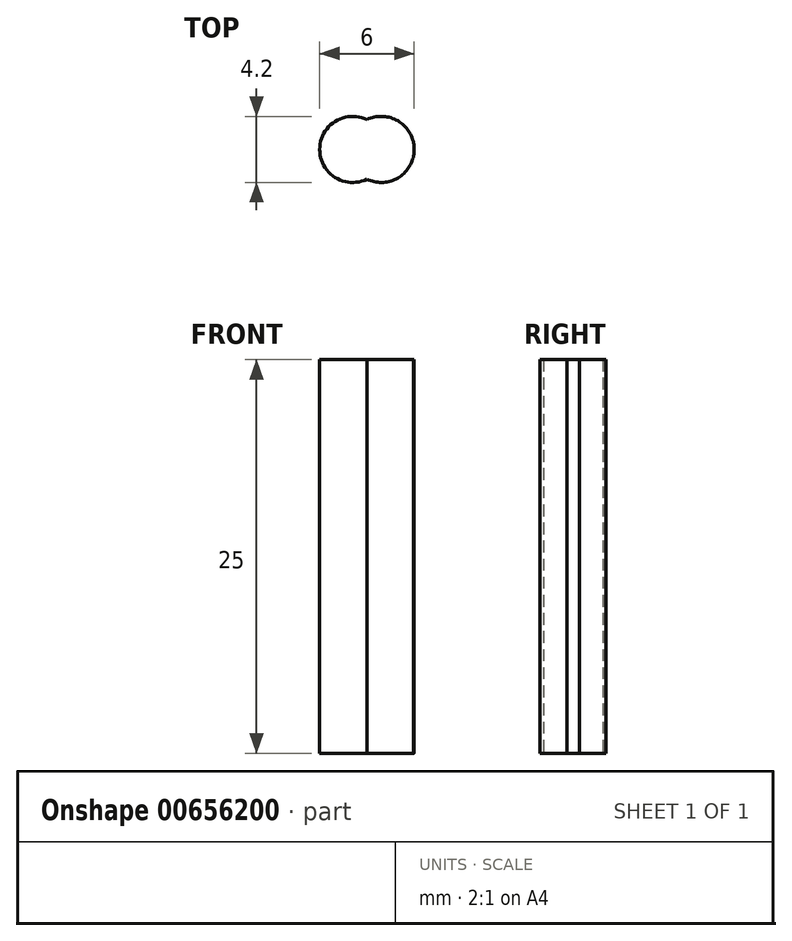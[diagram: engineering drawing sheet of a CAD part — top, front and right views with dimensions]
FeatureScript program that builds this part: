
annotation { "Feature Type Name" : "Feature", "Feature Type Description" : "" }
export const myFeature = defineFeature(function(context is Context, id is Id, definition is map)
    precondition{}
    {
        {
            var Q0;
            Q0=qCreatedBy(makeId("Top.planeOp"),FACE);
            var sketch = newSketch(context, id + "F0", { "sketchPlane" : qUnion([Q0])});
            skCircle(sketch, "E0", {"center": v(0, 0) * mm, "radius": 3 * mm});
            skCircle(sketch, "E1", {"center": v(-0.9, 0) * mm, "radius": 2.1 * mm});
            skCircle(sketch, "E2", {"center": v(0.91, 0) * mm, "radius": 2.1 * mm});
            skSolve(sketch);
        }
        {
            var Q0;
            {var subQ0=sQuery(id+"F0.wireOp",EDGE,"E2");var subQ1=sQuery(id+"F0.wireOp",EDGE,"E0");var subQ2=makeQuery(id+"F0.imprint","INTERSECT",VERTEX,{"disambiguationData":[OD(0.0)],"derivedFrom":[subQ1,subQ0]});Q0=makeQuery(id+"F0.imprint","IMPRINT",FACE,{"disambiguationData":[TD([[makeQuery(id+"F0.imprint","IMPRINT",EDGE,{"disambiguationData":[TD([[subQ2,1.0]])],"derivedFrom":subQ1}),1.0]])]});}
            var Q1;
            {var subQ0=sQuery(id+"F0.wireOp",EDGE,"E2");var subQ1=sQuery(id+"F0.wireOp",EDGE,"E1");var subQ2=makeQuery(id+"F0.imprint","INTERSECT",VERTEX,{"disambiguationData":[OD(0.0)],"derivedFrom":[subQ1,subQ0]});Q1=makeQuery(id+"F0.imprint","IMPRINT",FACE,{"disambiguationData":[TD([[makeQuery(id+"F0.imprint","IMPRINT",EDGE,{"disambiguationData":[TD([[subQ2,-1.0]])],"derivedFrom":subQ1}),1.0]])]});}
            var Q2;
            {var subQ0=sQuery(id+"F0.wireOp",EDGE,"E2");var subQ1=sQuery(id+"F0.wireOp",EDGE,"E1");var subQ2=makeQuery(id+"F0.imprint","INTERSECT",VERTEX,{"disambiguationData":[OD(0.0)],"derivedFrom":[subQ1,subQ0]});Q2=makeQuery(id+"F0.imprint","IMPRINT",FACE,{"disambiguationData":[TD([[makeQuery(id+"F0.imprint","IMPRINT",EDGE,{"disambiguationData":[TD([[subQ2,1.0]])],"derivedFrom":subQ1}),1.0]])]});}
            extrude(context, id + "F1", {"entities" : qUnion([Q0, Q1, Q2]), "depth" : 25 * mm, "offsetDistance" : 25 * mm});
        }
    });
